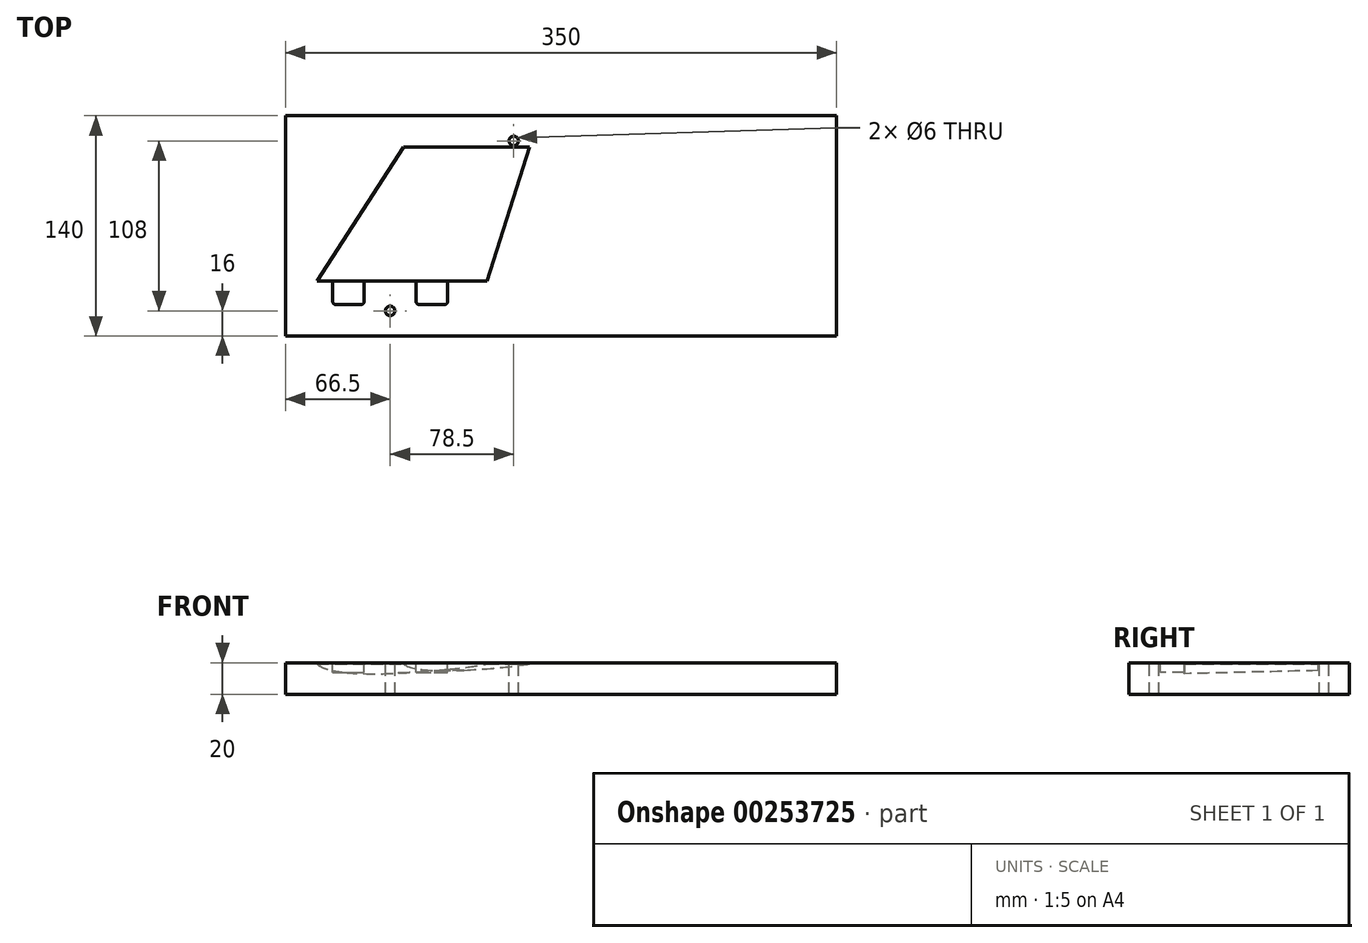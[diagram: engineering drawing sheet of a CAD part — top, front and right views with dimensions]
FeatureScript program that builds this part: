
annotation { "Feature Type Name" : "Feature", "Feature Type Description" : "" }
export const myFeature = defineFeature(function(context is Context, id is Id, definition is map)
    precondition{}
    {
        {
            var Q0;
            Q0=qCreatedBy(makeId("Top.planeOp"),FACE);
            var sketch = newSketch(context, id + "F0", { "sketchPlane" : qUnion([Q0])});
            skLineSegment(sketch, "E0.bottom", {"start": v(0, 0) * mm, "end": v(350, 0) * mm});
            skLineSegment(sketch, "E0.top", {"start": v(0, 140) * mm, "end": v(350, 140) * mm});
            skLineSegment(sketch, "E0.left", {"start": v(0, 0) * mm, "end": v(0, 140) * mm});
            skLineSegment(sketch, "E0.right", {"start": v(350, 0) * mm, "end": v(350, 140) * mm});
            skLineSegment(sketch, "E1", {"start": v(175, 140) * mm, "end": v(175, 0) * mm, "construction": true});
            skSolve(sketch);
        }
        {
            var Q0;
            Q0 = qSketchRegion(id + "F0", true);
            extrude(context, id + "F1", {"entities" : qUnion([Q0]), "oppositeDirection" : true, "depth" : 20 * mm});
        }
        {
            var Q0;
            Q0=makeQuery(id+"F1.opExtrude","CAP_FACE",FACE,{"disambiguationData":[OSD([sQuery(id+"F0.wireOp",EDGE,"E0.bottom"),sQuery(id+"F0.wireOp",EDGE,"E0.top"),sQuery(id+"F0.wireOp",EDGE,"E0.left"),sQuery(id+"F0.wireOp",EDGE,"E0.right")])],"isStart":true});
            var sketch = newSketch(context, id + "F2", { "sketchPlane" : qUnion([Q0])});
            skLineSegment(sketch, "E2", {"start": v(175, 140) * mm, "end": v(175, 0) * mm, "construction": true});
            skLineSegment(sketch, "E3.bottom", {"start": v(10, 130) * mm, "end": v(340, 130) * mm, "construction": true});
            skLineSegment(sketch, "E3.top", {"start": v(10, 10) * mm, "end": v(340, 10) * mm, "construction": true});
            skLineSegment(sketch, "E3.left", {"start": v(10, 130) * mm, "end": v(10, 10) * mm, "construction": true});
            skLineSegment(sketch, "E3.right", {"start": v(340, 130) * mm, "end": v(340, 10) * mm, "construction": true});
            skLineSegment(sketch, "E4", {"start": v(165, 130) * mm, "end": v(165, 10) * mm, "construction": true});
            skLineSegment(sketch, "E5.bottom", {"start": v(20, 120) * mm, "end": v(155, 120) * mm, "construction": true});
            skLineSegment(sketch, "E5.top", {"start": v(20, 20) * mm, "end": v(155, 20) * mm, "construction": true});
            skLineSegment(sketch, "E5.left", {"start": v(20, 120) * mm, "end": v(20, 20) * mm, "construction": true});
            skLineSegment(sketch, "E5.right", {"start": v(155, 120) * mm, "end": v(155, 20) * mm, "construction": true});
            skLineSegment(sketch, "E6", {"start": v(20, 35) * mm, "end": v(155, 35) * mm, "construction": true});
            skLineSegment(sketch, "E7", {"start": v(20, 35) * mm, "end": v(75, 120) * mm});
            skLineSegment(sketch, "E8", {"start": v(75, 120) * mm, "end": v(155, 120) * mm});
            skLineSegment(sketch, "E9", {"start": v(155, 120) * mm, "end": v(128, 35) * mm});
            skLineSegment(sketch, "E10.bottom", {"start": v(30, 35) * mm, "end": v(50, 35) * mm});
            skLineSegment(sketch, "E10.top", {"start": v(30, 20) * mm, "end": v(50, 20) * mm});
            skLineSegment(sketch, "E10.left", {"start": v(30, 35) * mm, "end": v(30, 20) * mm});
            skLineSegment(sketch, "E10.right", {"start": v(50, 35) * mm, "end": v(50, 20) * mm});
            skLineSegment(sketch, "E11.bottom", {"start": v(83, 35) * mm, "end": v(103, 35) * mm});
            skLineSegment(sketch, "E11.top", {"start": v(83, 20) * mm, "end": v(103, 20) * mm});
            skLineSegment(sketch, "E11.left", {"start": v(83, 35) * mm, "end": v(83, 20) * mm});
            skLineSegment(sketch, "E11.right", {"start": v(103, 35) * mm, "end": v(103, 20) * mm});
            skLineSegment(sketch, "E12", {"start": v(20, 35) * mm, "end": v(30, 35) * mm});
            skLineSegment(sketch, "E13", {"start": v(103, 35) * mm, "end": v(128, 35) * mm});
            skSolve(sketch);
        }
        {
            var Q0;
            Q0=qCreatedBy(makeId("Front.planeOp"),FACE);
            var Q1;
            Q1=sQuery(id+"F2.wireOp",VERTEX,"E6.start");
            cPlane(context, id + "F3", {"entities" : qUnion([Q0, Q1]), "cplaneType" : CPlaneType.PLANE_POINT, "offset" : 25 * mm, "width" : 150 * mm, "height" : 150 * mm});
        }
        {
            var Q0;
            Q0=qCreatedBy(id+"F3.planeOp",FACE);
            var sketch = newSketch(context, id + "F4", { "sketchPlane" : qUnion([Q0])});
            skPoint(sketch, "E14.0", {"position": v(20, 0) * mm});
            skPoint(sketch, "E14.1", {"position": v(128, 0) * mm});
            skLineSegment(sketch, "E15", {"start": v(20, 0) * mm, "end": v(128, 0) * mm});
            skLineSegment(sketch, "E16", {"start": v(20, -7) * mm, "end": v(130.18, -7) * mm, "construction": true});
            skLineSegment(sketch, "E17", {"start": v(20, 0) * mm, "end": v(20, -0.8) * mm});
            skLineSegment(sketch, "E18", {"start": v(128, 0) * mm, "end": v(128, -0.8) * mm});
            skFitSpline(sketch, "E19", {"points": [v(20, -0.8) * mm, v(128, -0.8) * mm], "startDerivative": vector(40.62, -38.04) * mm, "endDerivative": vector(34.01, 7.1) * mm});
            skSolve(sketch);
        }
        {
            var Q0;
            Q0=qCreatedBy(makeId("Front.planeOp"),FACE);
            var Q1;
            Q1=sQuery(id+"F2.wireOp",VERTEX,"E5.right.start");
            cPlane(context, id + "F5", {"entities" : qUnion([Q0, Q1]), "cplaneType" : CPlaneType.PLANE_POINT, "offset" : 25 * mm, "width" : 150 * mm, "height" : 150 * mm});
        }
        {
            var Q0;
            Q0=qCreatedBy(id+"F5.planeOp",FACE);
            var sketch = newSketch(context, id + "F6", { "sketchPlane" : qUnion([Q0])});
            skPoint(sketch, "E20.0", {"position": v(75, 0) * mm});
            skLineSegment(sketch, "E20.1", {"start": v(75, 0) * mm, "end": v(155, 0) * mm});
            skLineSegment(sketch, "E21", {"start": v(75, 0) * mm, "end": v(75, -0.8) * mm});
            skLineSegment(sketch, "E22", {"start": v(155, 0) * mm, "end": v(155, -0.8) * mm});
            skLineSegment(sketch, "E23", {"start": v(75, -5) * mm, "end": v(151.64, -5) * mm, "construction": true});
            skFitSpline(sketch, "E24", {"points": [v(75, -0.8) * mm, v(155, -0.8) * mm], "startDerivative": vector(26.46, -23.64) * mm, "endDerivative": vector(53.16, 8.29) * mm});
            skSolve(sketch);
        }
        {
            var Q1;
            Q1 = qSketchRegion(id + "F4", true);
            var Q2;
            Q2 = qSketchRegion(id + "F6", true);
            loft(context, id + "F7", {"operationType" : NewBodyOperationType.REMOVE, "sheetProfilesArray" : [{ "sheetProfileEntities" : qUnion([Q1]) }, { "sheetProfileEntities" : qUnion([Q2]) }]});
        }
        {
            var Q0;
            Q0=qCreatedBy(makeId("Top.planeOp"),FACE);
            var sketch = newSketch(context, id + "F8", { "sketchPlane" : qUnion([Q0])});
            skPoint(sketch, "E25.0", {"position": v(30, 35) * mm});
            skPoint(sketch, "E26.0", {"position": v(50, 20) * mm});
            skPoint(sketch, "E27.0", {"position": v(83, 35) * mm});
            skPoint(sketch, "E28.0", {"position": v(103, 20) * mm});
            skLineSegment(sketch, "E29.bottom", {"start": v(30, 35) * mm, "end": v(50, 35) * mm});
            skLineSegment(sketch, "E29.top", {"start": v(32, 20) * mm, "end": v(48, 20) * mm});
            skLineSegment(sketch, "E29.left", {"start": v(30, 35) * mm, "end": v(30, 22) * mm});
            skLineSegment(sketch, "E29.right", {"start": v(50, 35) * mm, "end": v(50, 22) * mm});
            skLineSegment(sketch, "E30.bottom", {"start": v(83, 35) * mm, "end": v(103, 35) * mm});
            skLineSegment(sketch, "E30.top", {"start": v(85, 20) * mm, "end": v(101, 20) * mm});
            skLineSegment(sketch, "E30.left", {"start": v(83, 35) * mm, "end": v(83, 22) * mm});
            skLineSegment(sketch, "E30.right", {"start": v(103, 35) * mm, "end": v(103, 22) * mm});
            skPoint(sketch, "E31.visualSharp", {"position": v(30, 20) * mm});
            skArc(sketch, "E31.filletArc", {"start": v(30, 22) * mm, "mid": v(30.59, 20.59) * mm, "end": v(32, 20) * mm});
            skArc(sketch, "E32.filletArc", {"start": v(48, 20) * mm, "mid": v(49.41, 20.59) * mm, "end": v(50, 22) * mm});
            skPoint(sketch, "E33.visualSharp", {"position": v(83, 20) * mm});
            skArc(sketch, "E33.filletArc", {"start": v(83, 22) * mm, "mid": v(83.59, 20.59) * mm, "end": v(85, 20) * mm});
            skArc(sketch, "E34.filletArc", {"start": v(101, 20) * mm, "mid": v(102.41, 20.59) * mm, "end": v(103, 22) * mm});
            skSolve(sketch);
        }
        {
            var Q0;
            Q0 = qSketchRegion(id + "F8", true);
            extrude(context, id + "F9", {"entities" : qUnion([Q0]), "operationType" : NewBodyOperationType.REMOVE, "oppositeDirection" : true, "depth" : 6.2 * mm});
        }
        {
            var Q0;
            Q0=makeQuery(id+"F2.imprint","IMPRINT",FACE,{"disambiguationData":[TD([[makeQuery(id+"F2.imprint","IMPRINT",EDGE,{"derivedFrom":sQuery(id+"F2.wireOp",EDGE,"E10.bottom")}),1.0]])]});
            var sketch = newSketch(context, id + "F10", { "sketchPlane" : qUnion([Q0])});
            skPoint(sketch, "E35", {"position": v(66.5, 16) * mm});
            skPoint(sketch, "E36", {"position": v(145, 124) * mm});
            skLineSegment(sketch, "E37", {"start": v(145, 124) * mm, "end": v(84.36, 124) * mm, "construction": true});
            skLineSegment(sketch, "E38", {"start": v(24.36, 16) * mm, "end": v(121.11, 16) * mm, "construction": true});
            skLineSegment(sketch, "E39", {"start": v(121.11, 16) * mm, "end": v(121.11, 36.35) * mm, "construction": true});
            skLineSegment(sketch, "E40", {"start": v(92.92, 16) * mm, "end": v(92.92, 20.97) * mm, "construction": true});
            skLineSegment(sketch, "E41", {"start": v(39.42, 16) * mm, "end": v(39.42, 21.29) * mm, "construction": true});
            skLineSegment(sketch, "E42", {"start": v(24.36, 16) * mm, "end": v(24.36, 36.03) * mm, "construction": true});
            skSolve(sketch);
        }
        {
            var Q0;
            Q0=sQuery(id+"F10.wireOp",VERTEX,"E35");
            var Q1;
            Q1=sQuery(id+"F10.wireOp",VERTEX,"E36");
            var Q2;
            Q2=makeQuery(id+"F1.opExtrude","SWEPT_BODY",BODY,{"disambiguationData":[OSD([sQuery(id+"F0.wireOp",EDGE,"E0.bottom"),sQuery(id+"F0.wireOp",EDGE,"E0.top"),sQuery(id+"F0.wireOp",EDGE,"E0.left"),sQuery(id+"F0.wireOp",EDGE,"E0.right")])]});
            hole(context, id + "F11", {"style" : HoleStyle.SIMPLE, "endStyle" : HoleEndStyle.THROUGH, "holeDiameter" : 6 * mm, "tappedDepth" : 12 * mm, "tapClearance" : 3, "locations" : qUnion([Q0, Q1]), "scope" : qUnion([Q2])});
        }
    });
